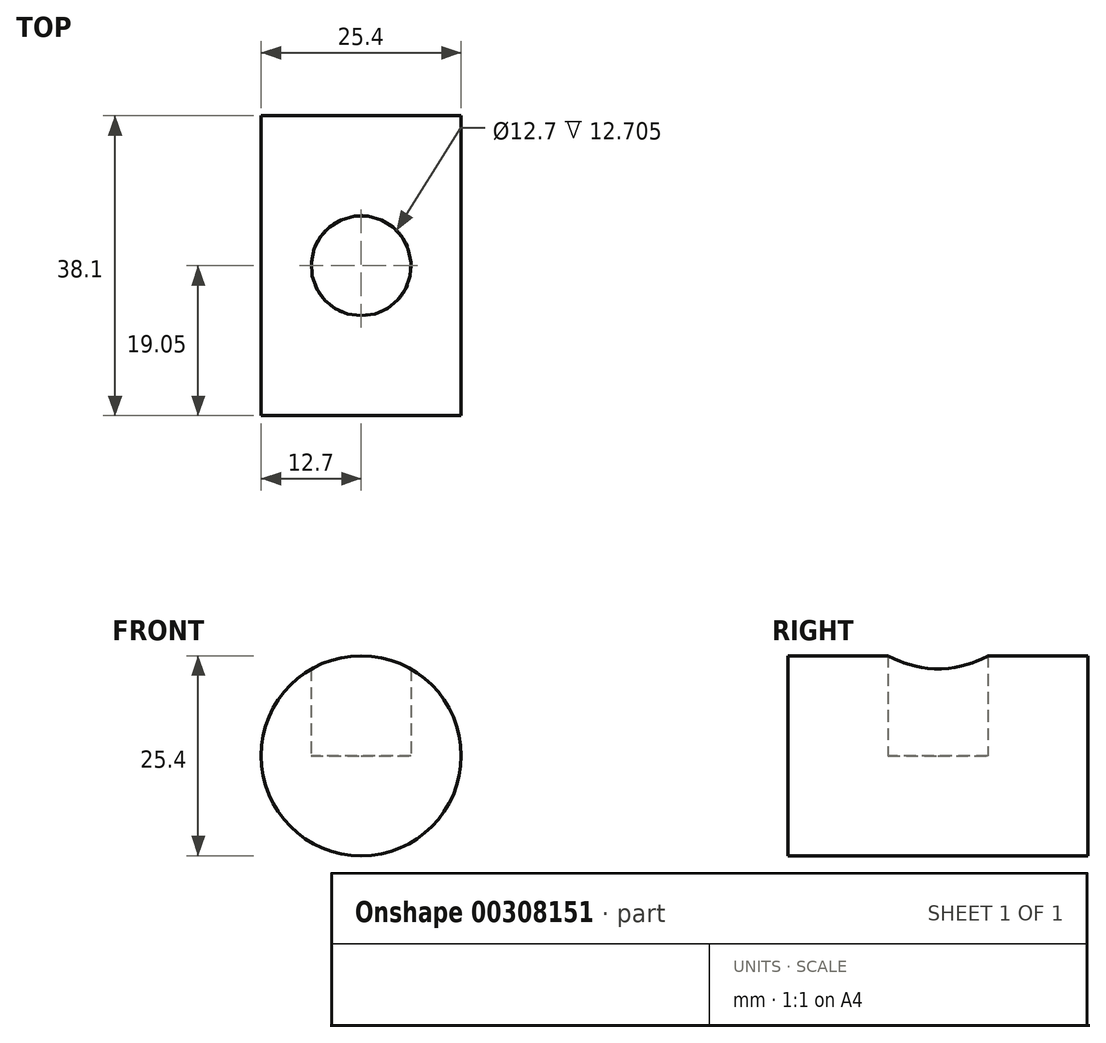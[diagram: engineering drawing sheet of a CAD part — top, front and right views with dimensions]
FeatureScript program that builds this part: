
annotation { "Feature Type Name" : "Feature", "Feature Type Description" : "" }
export const myFeature = defineFeature(function(context is Context, id is Id, definition is map)
    precondition{}
    {
        {
            var Q0;
            Q0=qCreatedBy(makeId("Front.planeOp"),FACE);
            var sketch = newSketch(context, id + "F0", { "sketchPlane" : qUnion([Q0])});
            skCircle(sketch, "E0", {"center": v(0, 0) * mm, "radius": 12.7 * mm});
            skSolve(sketch);
        }
        {
            var Q0;
            Q0 = qSketchRegion(id + "F0", true);
            var Q1;
            Q1 = qSketchRegion(id + "F2", true);
            extrude(context, id + "F1", {"entities" : qUnion([Q0, Q1]), "depth" : 38.1 * mm});
        }
        {
            var Q0;
            Q0=qCreatedBy(makeId("Top.planeOp"),FACE);
            var sketch = newSketch(context, id + "F2", { "sketchPlane" : qUnion([Q0])});
            skCircle(sketch, "E1", {"center": v(0, -19.05) * mm, "radius": 6.35 * mm});
            skSolve(sketch);
        }
        {
            var Q0;
            Q0 = qSketchRegion(id + "F2", true);
            extrude(context, id + "F3", {"entities" : qUnion([Q0]), "operationType" : NewBodyOperationType.REMOVE, "depth" : 12.7 * mm});
        }
    });
